FCSTD DOCUMENT  (FreeCAD 0.19R24415 (Git))
Label: uEFI_v3
License: All rights reserved
LicenseURL: http://en.wikipedia.org/wiki/All_rights_reserved
objects: Sketcher::SketchObject×1, PartDesign::Body×1
note: 2 computed .brp shape members not serialized (recipe doc carries the construction recipe); baked Part::Feature solids carry a one-line shape summary decoded from their .brp

FEATURE [Sketcher::SketchObject] Sketch
  FullyConstrained = false
  MapMode = 5
  Support = -> [XY_Plane]
  sketch-geometry (4):
    g0: LineSegment StartX=-48.0578 StartY=58.8355 StartZ=0 EndX=54.4422 EndY=58.8355 EndZ=0
    g1: LineSegment StartX=54.4422 StartY=58.8355 StartZ=0 EndX=54.4422 EndY=-65.1645 EndZ=0
    g2: LineSegment StartX=54.4422 StartY=-65.1645 StartZ=0 EndX=-48.0578 EndY=-65.1645 EndZ=0
    g3: LineSegment StartX=-48.0578 StartY=-65.1645 StartZ=0 EndX=-48.0578 EndY=58.8355 EndZ=0
  constraints (10):
    c: Coincident(g0,g1)
    c: Coincident(g1,g2)
    c: Coincident(g2,g3)
    c: Coincident(g3,g0)
    c: Horizontal(g0)
    c: Horizontal(g2)
    c: Vertical(g1)
    c: Vertical(g3)
    c: DistanceX(g0,g0) = 102.5
    c: DistanceY(g1,g1) = 124
FEATURE [PartDesign::Body] Body
  Group = -> [Sketch]
  Origin = -> Origin
